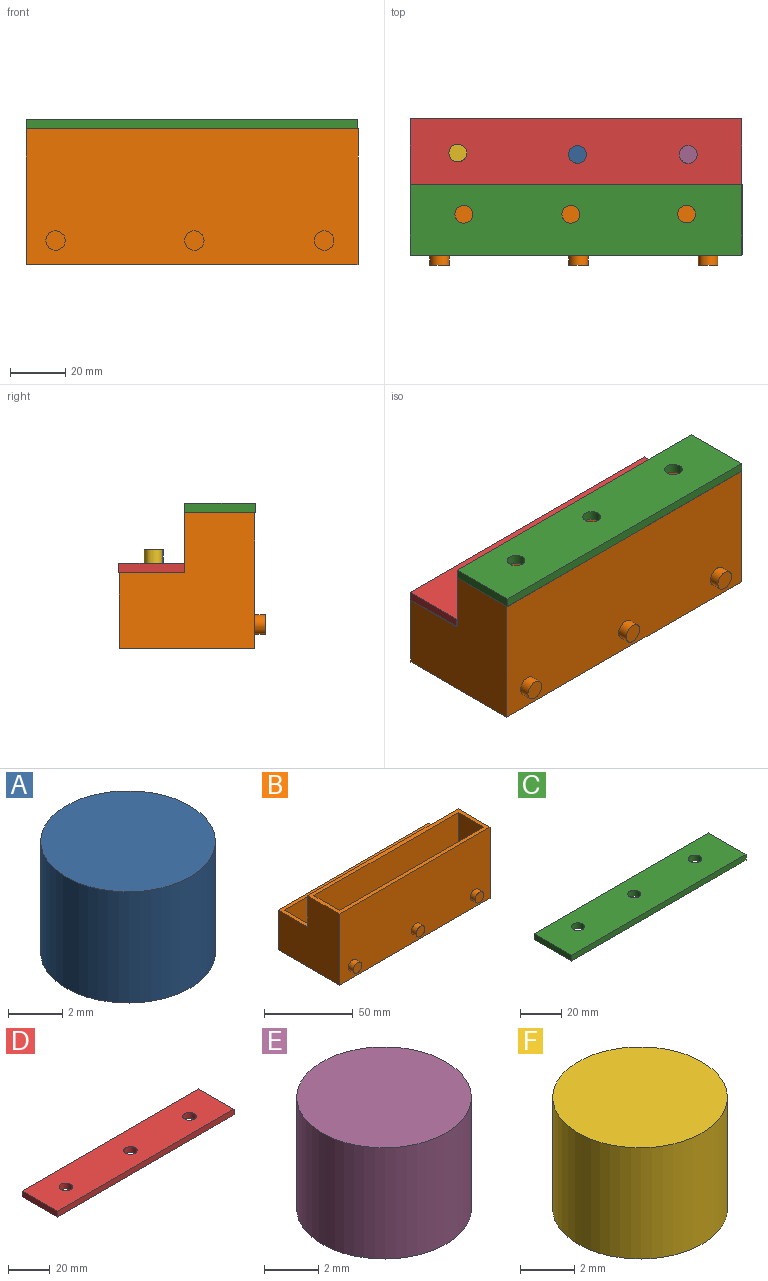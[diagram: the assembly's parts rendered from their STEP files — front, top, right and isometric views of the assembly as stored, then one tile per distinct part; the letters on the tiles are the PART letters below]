
ASSEMBLY  parts=6 mates=6
PART A: 3 faces, bbox 6.4x6.4x5 mm
  f0: cylinder r=3.21mm len=6.42mm, axis (0,0,-1), area 100.8mm2, adj f1,f2
  f1: plane 6.42x6.42mm, normal (0,0,1), area 32.4mm2, adj f0
  f2: plane 6.42x6.42mm, normal (0,0,-1), area 32.4mm2, adj f0
PART B: 38 faces, bbox 120x52.7x49.1 mm
  f0: plane 24.76x2.38mm, normal (0,-1,0), area 59mm2, adj f10,f23,f24,f25
  f1: plane 114.92x46.54mm, normal (0,-1,0), area 2492.8mm2, adj f5,f10,f11,f12,f18,f22
  f2: plane 39.55x26.08mm, normal (0,0,1), area 1031.5mm2, adj f21,f24,f26,f29
  f3: plane 33.96x26.08mm, normal (0,0,1), area 885.9mm2, adj f20,f21,f23,f31
  f4: plane 120x49.08mm, normal (0,1,0), area 2604.2mm2, adj f5,f6,f7,f8,f15,f17,f18
  f5: plane 120x25.4mm, normal (0,0,1), area 712.8mm2, adj f1,f4,f7,f8,f9,f11,f12,f13
  f6: plane 120x48.94mm, normal (0,0,-1), area 5870.9mm2, adj f4,f7,f8,f9,f16,f17
  f7: plane 49.08x25.4mm, normal (1,0,0), area 1246.7mm2, adj f4,f5,f6,f9
  f8: plane 49.08x48.94mm, normal (-1,0,0), area 1891.8mm2, adj f4,f5,f6,f9,f15,f16
  f9: plane 120x49.08mm, normal (0,-1,0), area 5774.3mm2, adj f5,f6,f7,f8,f32,f34,f36
  f10: plane 114.92x20.32mm, normal (0,0,1), area 2059.2mm2, adj f0,f1,f11,f12,f13,f14,f22,f23
  f11: plane 46.54x20.32mm, normal (-1,0,0), area 945.7mm2, adj f1,f5,f10,f13
  f12: plane 46.54x20.32mm, normal (1,0,0), area 883.6mm2, adj f1,f5,f10,f13,f18,f31
  f13: plane 114.92x46.54mm, normal (0,1,0), area 5348.5mm2, adj f5,f10,f11,f12
  f14: plane 24.76x2.1mm, normal (0,-1,0), area 51.9mm2, adj f10,f26,f27,f28
  f15: plane 119.9x23.54mm, normal (0,0,1), area 405mm2, adj f4,f8,f16,f17,f20,f21,f22
  f16: plane 119.9x27.4mm, normal (0,1,0), area 3285.5mm2, adj f6,f8,f15,f17
  f17: plane 27.4x23.54mm, normal (1,0,0), area 645.2mm2, adj f4,f6,f15,f16
  f18: plane 114.9x5.04mm, normal (0,0,-1), area 291.9mm2, adj f1,f4,f12,f20,f22,f31
  f19: plane 36.91x26.08mm, normal (0,0,1), area 962.8mm2, adj f21,f22,f27,f30
  f20: plane 26.08x24.9mm, normal (1,0,0), area 649.5mm2, adj f3,f15,f18,f21,f31
  f21: plane 114.9x24.9mm, normal (0,-1,0), area 2750.2mm2, adj f2,f3,f15,f19,f20,f22,f23,f24
  f22: plane 26.08x24.9mm, normal (-1,0,0), area 587.4mm2, adj f1,f10,f15,f18,f19,f21,f30
  f23: plane 26.08x24.8mm, normal (-1,0,0), area 585mm2, adj f0,f3,f10,f21,f25,f31
  f24: plane 26.08x24.8mm, normal (1,0,0), area 585mm2, adj f0,f2,f10,f21,f25,f29
  f25: plane 23.58x2.38mm, normal (0,0,1), area 56.2mm2, adj f0,f21,f23,f24
  f26: plane 26.08x24.8mm, normal (-1,0,0), area 585mm2, adj f2,f10,f14,f21,f28,f29
  f27: plane 26.08x24.8mm, normal (1,0,0), area 585mm2, adj f10,f14,f19,f21,f28,f30
  f28: plane 23.58x2.1mm, normal (0,0,1), area 49.4mm2, adj f14,f21,f26,f27
  f29: plane 39.55x0.04mm, normal (0,1,0), area 1.6mm2, adj f2,f10,f24,f26
  f30: plane 36.91x0.04mm, normal (0,1,0), area 1.5mm2, adj f10,f19,f22,f27
  f31: plane 33.96x24.9mm, normal (0,1,0), area 2.4mm2, adj f3,f10,f12,f18,f20,f23
  f32: cylinder r=3.5mm len=7mm, axis (0,1,0), area 83.6mm2, adj f9,f33
  f33: plane 7x7mm, normal (0,-1,0), area 38.5mm2, adj f32
  f34: cylinder r=3.5mm len=7mm, axis (0,1,0), area 83.6mm2, adj f9,f35
  f35: plane 7x7mm, normal (0,-1,0), area 38.5mm2, adj f34
  f36: cylinder r=3.5mm len=7mm, axis (0,1,0), area 83.6mm2, adj f9,f37
  f37: plane 7x7mm, normal (0,-1,0), area 38.5mm2, adj f36
PART C: 9 faces, bbox 120x25.6x3.4 mm
  f0: plane 25.64x3.4mm, normal (-1,0,0), area 87.2mm2, adj f1,f6,f7,f8
  f1: plane 120x3.4mm, normal (0,-1,0), area 408mm2, adj f0,f2,f7,f8
  f2: plane 25.64x3.4mm, normal (1,0,0), area 87.2mm2, adj f1,f6,f7,f8
  f3: cylinder r=3.21mm len=6.42mm, axis (0,0,-1), area 68.6mm2, adj f7,f8
  f4: cylinder r=3.21mm len=6.42mm, axis (0,0,-1), area 68.6mm2, adj f7,f8
  f5: cylinder r=3.21mm len=6.42mm, axis (0,0,-1), area 68.6mm2, adj f7,f8
  f6: plane 120x3.4mm, normal (0,1,0), area 408mm2, adj f0,f2,f7,f8
  f7: plane 120x25.64mm, normal (0,0,1), area 2979.7mm2, adj f0,f1,f2,f3,f4,f5,f6
  f8: plane 120x25.64mm, normal (0,0,-1), area 2979.7mm2, adj f0,f1,f2,f3,f4,f5,f6
PART D: 9 faces, bbox 120x23.8x3.4 mm
  f0: plane 23.8x3.4mm, normal (-1,0,0), area 80.9mm2, adj f1,f6,f7,f8
  f1: plane 120x3.4mm, normal (0,-1,0), area 408mm2, adj f0,f2,f7,f8
  f2: plane 23.8x3.4mm, normal (1,0,0), area 80.9mm2, adj f1,f6,f7,f8
  f3: cylinder r=3.21mm len=6.42mm, axis (0,0,-1), area 68.6mm2, adj f7,f8
  f4: cylinder r=3.21mm len=6.42mm, axis (0,0,-1), area 68.6mm2, adj f7,f8
  f5: cylinder r=3.21mm len=6.42mm, axis (0,0,-1), area 68.6mm2, adj f7,f8
  f6: plane 120x3.4mm, normal (0,1,0), area 408mm2, adj f0,f2,f7,f8
  f7: plane 120x23.8mm, normal (0,0,1), area 2758.9mm2, adj f0,f1,f2,f3,f4,f5,f6
  f8: plane 120x23.8mm, normal (0,0,-1), area 2758.9mm2, adj f0,f1,f2,f3,f4,f5,f6
PART E: 3 faces, bbox 6.4x6.4x5 mm
  f0: cylinder r=3.21mm len=6.42mm, axis (0,0,-1), area 100.8mm2, adj f1,f2
  f1: plane 6.42x6.42mm, normal (0,0,1), area 32.4mm2, adj f0
  f2: plane 6.42x6.42mm, normal (0,0,-1), area 32.4mm2, adj f0
PART F: 3 faces, bbox 6.4x6.4x5 mm
  f0: cylinder r=3.21mm len=6.42mm, axis (0,0,-1), area 100.8mm2, adj f1,f2
  f1: plane 6.42x6.42mm, normal (0,0,1), area 32.4mm2, adj f0
  f2: plane 6.42x6.42mm, normal (0,0,-1), area 32.4mm2, adj f0
PLACE A t=(3.75,-2.44,-58.07)mm
PLACE B t=(49.58,54.04,-61.47)mm
PLACE C t=(69.1,81.62,-39.79)mm
PLACE D t=(49.27,24.74,-61.47)mm
PLACE E t=(52.43,-2.94,-58.07)mm
PLACE F t=(-49.24,-1.46,-58.07)mm
MATE slider A.f0 <-> D.f4  axis (0,0,-1) through (49.27,64.89,-58.07)mm
MATE parallel C.f2 <-> B.f7  axis (1,0,0) through (108.78,54.04,-39.79)mm
MATE parallel D.f2 <-> B.f17  axis (1,0,0) through (108.68,54.04,-61.47)mm
MATE slider F.f0 <-> D.f3  axis (0,0,-1) through (5.95,65.4,-58.07)mm
MATE parallel B.f15 <-> B.f15  axis (0,0,1) through (108.68,54.04,-61.47)mm
MATE slider E.f0 <-> D.f5  axis (0,0,-1) through (89.32,64.89,-58.07)mm
